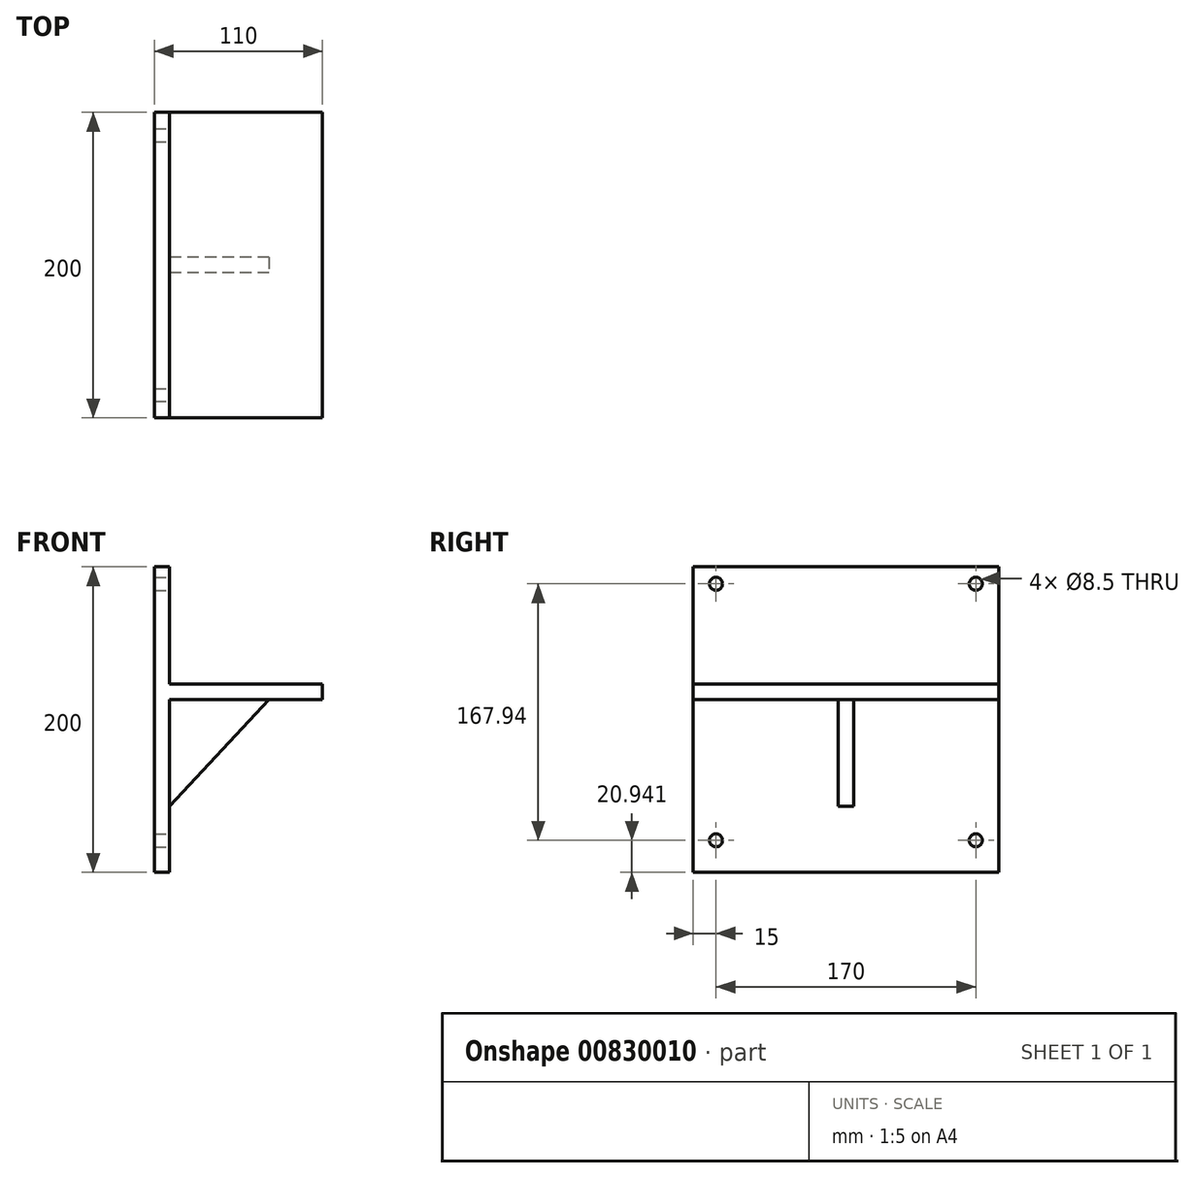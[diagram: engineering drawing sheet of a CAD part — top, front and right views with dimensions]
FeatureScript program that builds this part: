
annotation { "Feature Type Name" : "Feature", "Feature Type Description" : "" }
export const myFeature = defineFeature(function(context is Context, id is Id, definition is map)
    precondition{}
    {
        {
            var Q0;
            Q0=qCreatedBy(makeId("Front.planeOp"),FACE);
            var sketch = newSketch(context, id + "F0", { "sketchPlane" : qUnion([Q0])});
            skLineSegment(sketch, "E0.bottom", {"start": v(-5, 100) * mm, "end": v(5, 100) * mm});
            skLineSegment(sketch, "E0.top", {"start": v(-5, -100) * mm, "end": v(5, -100) * mm});
            skLineSegment(sketch, "E0.left", {"start": v(-5, 100) * mm, "end": v(-5, -100) * mm});
            skLineSegment(sketch, "E0.right", {"start": v(5, 100) * mm, "end": v(5, 23.2) * mm});
            skPoint(sketch, "E0.middle", {"position": v(0, 0) * mm});
            skLineSegment(sketch, "E1", {"start": v(-5, -100) * mm, "end": v(-5, 13.2) * mm});
            skLineSegment(sketch, "E2", {"start": v(-5, -100) * mm, "end": v(-5, 23.2) * mm});
            skLineSegment(sketch, "E3.bottom", {"start": v(-5, 23.2) * mm, "end": v(-5, 23.2) * mm});
            skLineSegment(sketch, "E3.top", {"start": v(-5, 13.2) * mm, "end": v(-5, 13.2) * mm});
            skLineSegment(sketch, "E3.left", {"start": v(-5, 23.2) * mm, "end": v(-5, 13.2) * mm});
            skLineSegment(sketch, "E3.right", {"start": v(-5, 23.2) * mm, "end": v(-5, 13.2) * mm});
            skLineSegment(sketch, "E4.bottom", {"start": v(105, 23.2) * mm, "end": v(5, 23.2) * mm});
            skLineSegment(sketch, "E4.top", {"start": v(105, 13.2) * mm, "end": v(5, 13.2) * mm});
            skLineSegment(sketch, "E4.left", {"start": v(105, 23.2) * mm, "end": v(105, 13.2) * mm});
            skLineSegment(sketch, "E5.trimOffspring", {"start": v(5, 13.2) * mm, "end": v(5, -100) * mm});
            skSolve(sketch);
        }
        {
            var Q0;
            Q0 = qSketchRegion(id + "F0", true);
            extrude(context, id + "F1", {"entities" : qUnion([Q0]), "depth" : 200 * mm, "offsetDistance" : 25 * mm});
        }
        {
            var Q0;
            Q0=qCreatedBy(makeId("Right.planeOp"),FACE);
            var sketch = newSketch(context, id + "F2", { "sketchPlane" : qUnion([Q0])});
            skLineSegment(sketch, "E6", {"start": v(0, 0) * mm, "end": v(0, 13.2) * mm});
            skLineSegment(sketch, "E7", {"start": v(0, 13.2) * mm, "end": v(-95, 13.2) * mm});
            skLineSegment(sketch, "E8", {"start": v(-95, 13.2) * mm, "end": v(-105, 13.2) * mm});
            skLineSegment(sketch, "E9.bottom", {"start": v(-105, 13.2) * mm, "end": v(-95, 13.2) * mm});
            skLineSegment(sketch, "E9.top", {"start": v(-105, -100) * mm, "end": v(-95, -100) * mm});
            skLineSegment(sketch, "E10", {"start": v(-95, 13.2) * mm, "end": v(-95, -56.8) * mm});
            skLineSegment(sketch, "E11.top", {"start": v(-105, -56.8) * mm, "end": v(-95, -56.8) * mm});
            skLineSegment(sketch, "E11.left", {"start": v(-105, 13.2) * mm, "end": v(-105, -56.8) * mm});
            skLineSegment(sketch, "E12", {"start": v(-185, 88.88) * mm, "end": v(-180.75, 88.88) * mm});
            skLineSegment(sketch, "E13", {"start": v(-185, 88.88) * mm, "end": v(-185, 84.63) * mm});
            skLineSegment(sketch, "E14", {"start": v(-185, -79.06) * mm, "end": v(-180.75, -79.06) * mm});
            skLineSegment(sketch, "E15", {"start": v(-15, -79.06) * mm, "end": v(-15, -74.8) * mm});
            skCircle(sketch, "E16", {"center": v(-185, 88.88) * mm, "radius": 4.25 * mm});
            skCircle(sketch, "E17", {"center": v(-15, 88.88) * mm, "radius": 4.25 * mm});
            skCircle(sketch, "E18", {"center": v(-15, -79.06) * mm, "radius": 4.25 * mm});
            skCircle(sketch, "E19", {"center": v(-185, -79.06) * mm, "radius": 4.25 * mm});
            skLineSegment(sketch, "E20.trimOffspring", {"start": v(-19.25, 88.88) * mm, "end": v(-15, 88.88) * mm});
            skLineSegment(sketch, "E21.trimOffspring", {"start": v(-185, -74.8) * mm, "end": v(-185, -79.06) * mm});
            skLineSegment(sketch, "E22.trimOffspring", {"start": v(-19.25, -79.06) * mm, "end": v(-15, -79.06) * mm});
            skLineSegment(sketch, "E23.trimOffspring", {"start": v(-15, 84.63) * mm, "end": v(-15, 88.88) * mm});
            skSolve(sketch);
        }
        {
            var Q0;
            Q0 = qSketchRegion(id + "F2", true);
            extrude(context, id + "F3", {"entities" : qUnion([Q0]), "operationType" : NewBodyOperationType.ADD, "depth" : 70 * mm, "offsetDistance" : 25 * mm});
        }
        {
            var Q0;
            Q0=makeQuery(id+"F3.opExtrude","SWEPT_FACE",FACE,{"disambiguationData":[OSD([sQuery(id+"F2.wireOp",EDGE,"E11.left")])]});
            var sketch = newSketch(context, id + "F4", { "sketchPlane" : qUnion([Q0])});
            skLineSegment(sketch, "E24", {"start": v(70, -56.8) * mm, "end": v(5, -56.8) * mm});
            skLineSegment(sketch, "E25", {"start": v(5, -56.8) * mm, "end": v(70, 13.2) * mm});
            skLineSegment(sketch, "E26", {"start": v(70, 13.2) * mm, "end": v(70, -56.8) * mm});
            skSolve(sketch);
        }
        {
            var Q0;
            Q0=makeQuery(id+"F4.imprint","IMPRINT",FACE,{"disambiguationData":[TD([[makeQuery(id+"F4.imprint","IMPRINT",EDGE,{"derivedFrom":sQuery(id+"F4.wireOp",EDGE,"E24")}),-1.0]])]});
            extrude(context, id + "F5", {"entities" : qUnion([Q0]), "operationType" : NewBodyOperationType.REMOVE, "oppositeDirection" : true, "depth" : 100 * mm, "offsetDistance" : 25 * mm});
        }
        {
            var Q0;
            Q0=makeQuery(id+"F3.opExtrude","CAP_FACE",FACE,{"disambiguationData":[OSD([sQuery(id+"F2.wireOp",EDGE,"E16")])],"isStart":false});
            var Q1;
            Q1=makeQuery(id+"F3.opExtrude","CAP_FACE",FACE,{"disambiguationData":[OSD([sQuery(id+"F2.wireOp",EDGE,"E17")])],"isStart":false});
            var Q2;
            Q2=makeQuery(id+"F3.opExtrude","CAP_FACE",FACE,{"disambiguationData":[OSD([sQuery(id+"F2.wireOp",EDGE,"E18")])],"isStart":false});
            var Q3;
            Q3=makeQuery(id+"F3.opExtrude","CAP_FACE",FACE,{"disambiguationData":[OSD([sQuery(id+"F2.wireOp",EDGE,"E19")])],"isStart":false});
            extrude(context, id + "F6", {"entities" : qUnion([Q0, Q1, Q2, Q3]), "operationType" : NewBodyOperationType.REMOVE, "endBound" : BoundingType.THROUGH_ALL, "oppositeDirection" : true, "depth" : 25 * mm, "offsetDistance" : 25 * mm});
        }
    });
